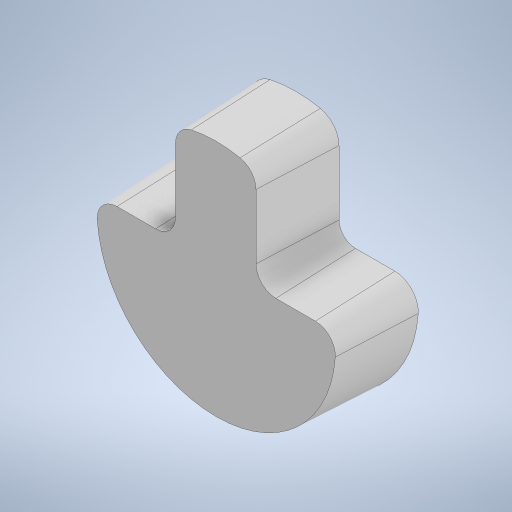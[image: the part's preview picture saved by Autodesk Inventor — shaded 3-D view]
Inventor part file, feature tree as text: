
AUTODESK INVENTOR PART (.ipt)
format: ipt  version: 2023 (Build 270158000, 158)  size: 261,120 bytes
history: native  units: in
note: dims shown in document units (in); Inventor stores cm internally (conversion verified against a paired STEP export)
features: extrude x1, draft x1, sketch x1
ambient origin geometry x8: Origin, YZ Plane, XZ Plane, XY Plane, X Axis, Y Axis, Z Axis, Center Point
bodies: Solid1 (feature_tree)
feature tree (3):
  extrude  "Extrusion1"  Depth=0.5in
  draft  "FaceDraft1"
  sketch  "Sketch1"  dims[d2=1.5in d3=0.25in d6=0.25in d7=0.5in d8=0.0in d11=0.625in d12=0.125in d13=0.0172in d10=0.5in]
